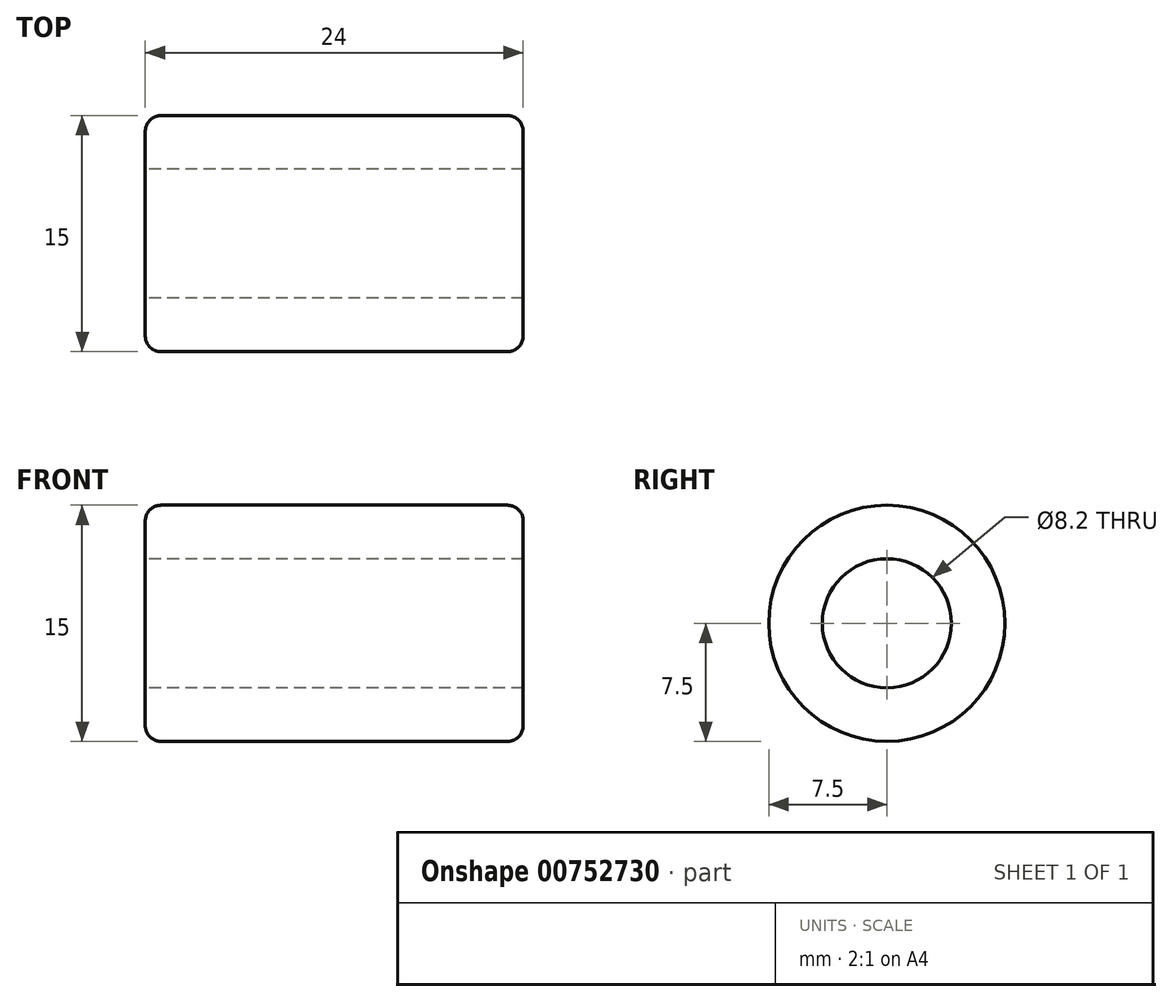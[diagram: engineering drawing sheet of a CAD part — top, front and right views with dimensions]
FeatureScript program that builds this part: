
annotation { "Feature Type Name" : "Feature", "Feature Type Description" : "" }
export const myFeature = defineFeature(function(context is Context, id is Id, definition is map)
    precondition{}
    {
        {
            var Q0;
            Q0=qCreatedBy(makeId("Front.planeOp"),FACE);
            var sketch = newSketch(context, id + "F0", { "sketchPlane" : qUnion([Q0])});
            skLineSegment(sketch, "E0.bottom", {"start": v(-11, 7.5) * mm, "end": v(11, 7.5) * mm});
            skLineSegment(sketch, "E0.top", {"start": v(-11, -7.5) * mm, "end": v(11, -7.5) * mm});
            skLineSegment(sketch, "E0.left", {"start": v(-12, 6.5) * mm, "end": v(-12, -6.5) * mm});
            skLineSegment(sketch, "E0.right", {"start": v(12, 6.5) * mm, "end": v(12, -6.5) * mm});
            skPoint(sketch, "E0.middle", {"position": v(0, 0) * mm});
            skLineSegment(sketch, "E1", {"start": v(-12, 0) * mm, "end": v(12, 0) * mm});
            skLineSegment(sketch, "E2", {"start": v(-12, 4.1) * mm, "end": v(12, 4.1) * mm});
            skPoint(sketch, "E3.visualSharp", {"position": v(-12, 7.5) * mm});
            skArc(sketch, "E3.filletArc", {"start": v(-11, 7.5) * mm, "mid": v(-11.7, 7.2) * mm, "end": v(-12, 6.5) * mm});
            skPoint(sketch, "E4.visualSharp", {"position": v(12, 7.5) * mm});
            skArc(sketch, "E4.filletArc", {"start": v(12, 6.5) * mm, "mid": v(11.7, 7.2) * mm, "end": v(11, 7.5) * mm});
            skPoint(sketch, "E5.visualSharp", {"position": v(12, -7.5) * mm});
            skArc(sketch, "E5.filletArc", {"start": v(11, -7.5) * mm, "mid": v(11.7, -7.2) * mm, "end": v(12, -6.5) * mm});
            skPoint(sketch, "E6.visualSharp", {"position": v(-12, -7.5) * mm});
            skArc(sketch, "E6.filletArc", {"start": v(-12, -6.5) * mm, "mid": v(-11.7, -7.2) * mm, "end": v(-11, -7.5) * mm});
            skSolve(sketch);
        }
        {
            var Q0;
            {var subQ0=sQuery(id+"F0.wireOp",EDGE,"E0.bottom");Q0=makeQuery(id+"F0.imprint","IMPRINT",FACE,{"disambiguationData":[TD([[makeQuery(id+"F0.imprint","IMPRINT",EDGE,{"derivedFrom":subQ0}),-1.0]])]});}
            var Q1;
            Q1=sQuery(id+"F0.wireOp",EDGE,"E1");
            revolve(context, id + "F1", {"surfaceOperationType" : NewSurfaceOperationType.NEW, "entities" : qUnion([Q0]), "axis" : qUnion([Q1]), "revolveType" : RevolveType.FULL});
        }
    });
